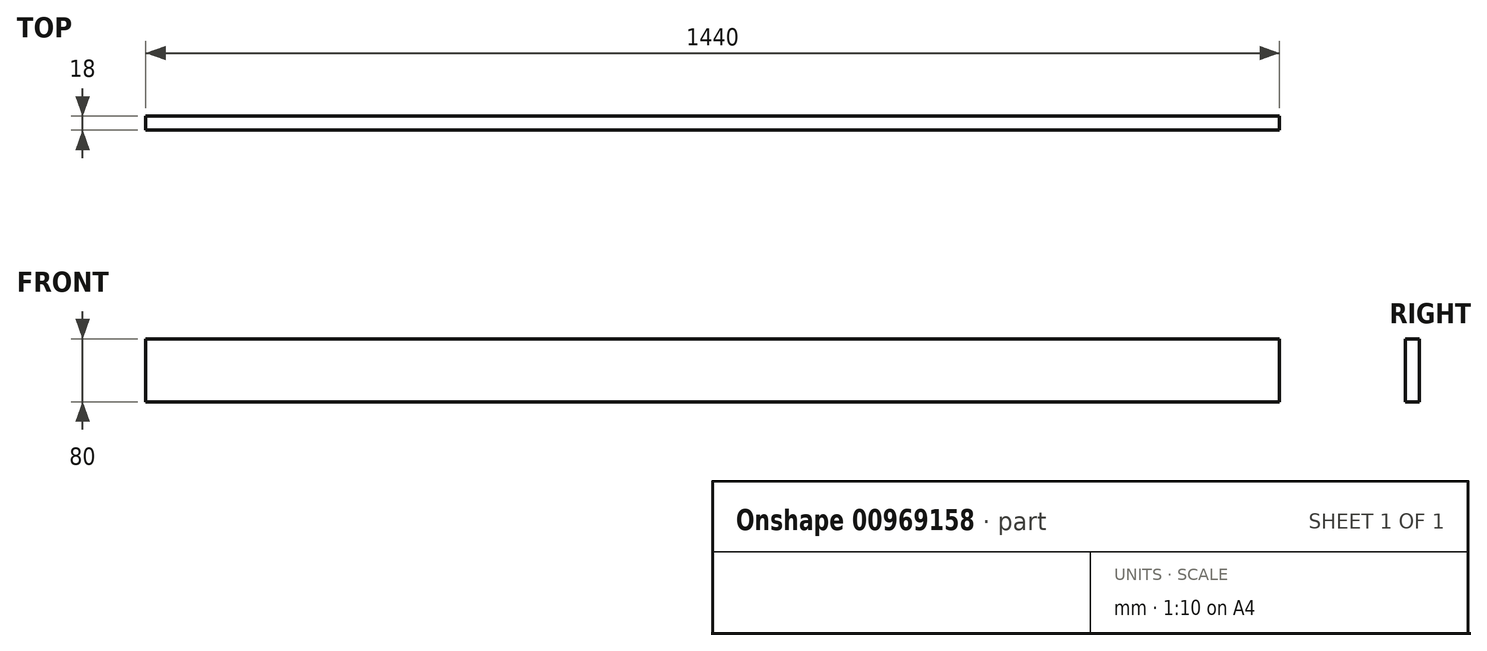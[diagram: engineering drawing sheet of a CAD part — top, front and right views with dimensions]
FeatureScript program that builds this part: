
annotation { "Feature Type Name" : "Feature", "Feature Type Description" : "" }
export const myFeature = defineFeature(function(context is Context, id is Id, definition is map)
    precondition{}
    {
        {
            var Q0;
            Q0=qCreatedBy(makeId("Front.planeOp"),FACE);
            var sketch = newSketch(context, id + "F0", { "sketchPlane" : qUnion([Q0])});
            skLineSegment(sketch, "E0.bottom", {"start": v(0, 0) * mm, "end": v(1440, 0) * mm});
            skLineSegment(sketch, "E0.top", {"start": v(0, 80) * mm, "end": v(1440, 80) * mm});
            skLineSegment(sketch, "E0.left", {"start": v(0, 0) * mm, "end": v(0, 80) * mm});
            skLineSegment(sketch, "E0.right", {"start": v(1440, 0) * mm, "end": v(1440, 80) * mm});
            skSolve(sketch);
        }
        {
            var Q0;
            Q0 = qSketchRegion(id + "F0", true);
            extrude(context, id + "F1", {"entities" : qUnion([Q0]), "depth" : 18 * mm, "offsetDistance" : 25 * mm});
        }
    });
